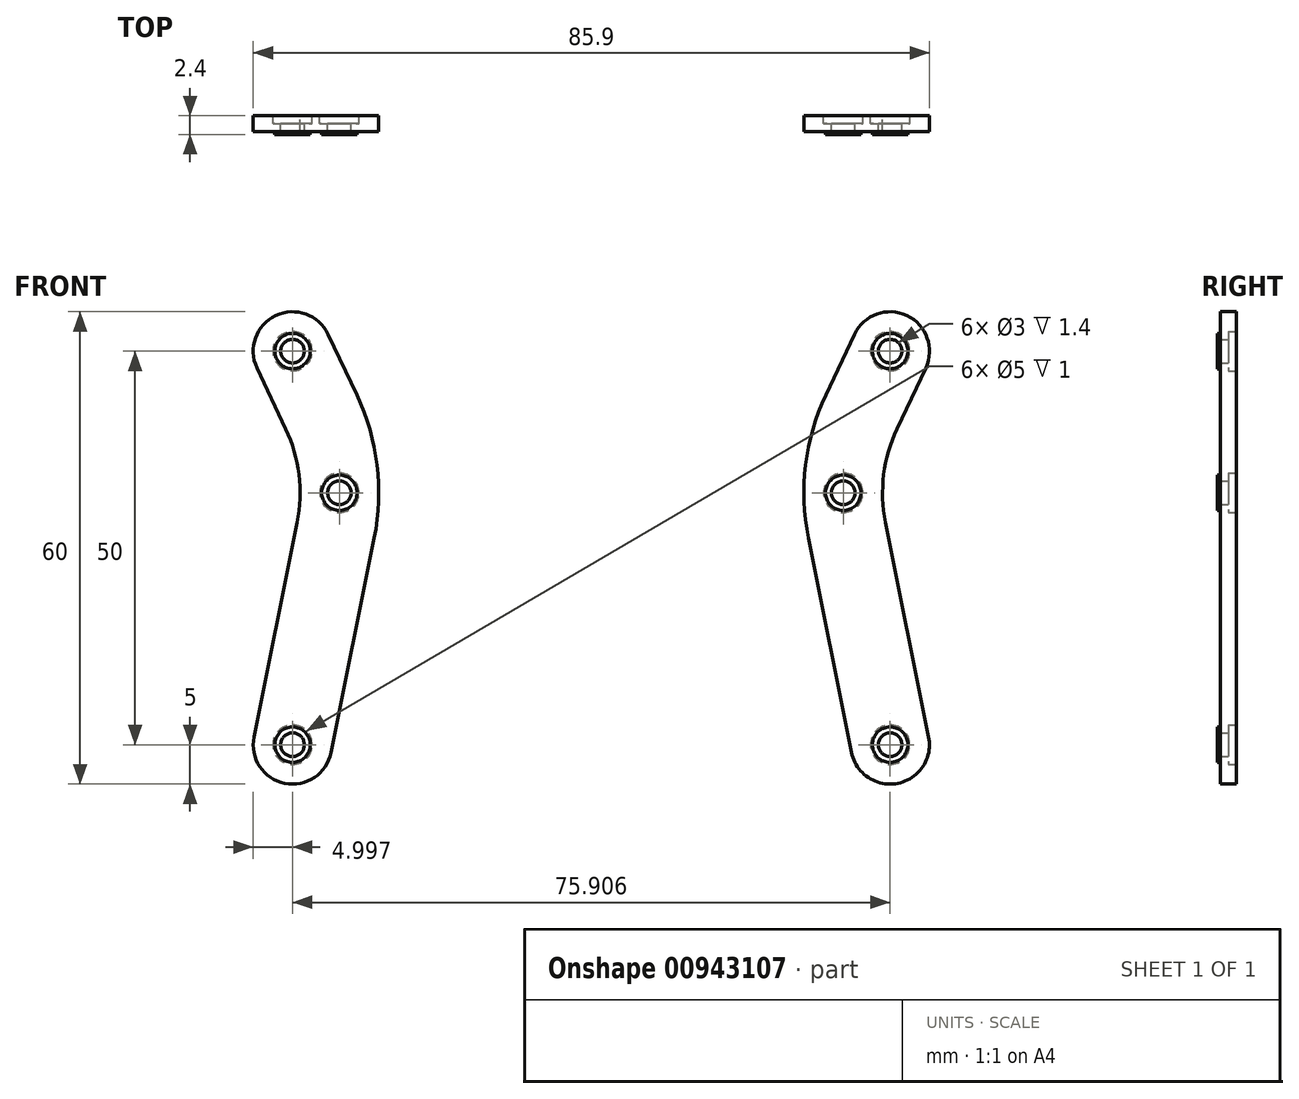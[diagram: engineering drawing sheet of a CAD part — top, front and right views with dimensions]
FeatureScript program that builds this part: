
annotation { "Feature Type Name" : "Feature", "Feature Type Description" : "" }
export const myFeature = defineFeature(function(context is Context, id is Id, definition is map)
    precondition{}
    {
        {
            var Q0;
            Q0=qCreatedBy(makeId("Front.planeOp"),FACE);
            var sketch = newSketch(context, id + "F0", { "sketchPlane" : qUnion([Q0])});
            skLineSegment(sketch, "E0", {"start": v(5.95, -32) * mm, "end": v(0.47, -4.74) * mm});
            skLineSegment(sketch, "E1", {"start": v(2.3, 10.26) * mm, "end": v(5.95, 18) * mm});
            skArc(sketch, "E2", {"start": v(2.3, 10.26) * mm, "mid": v(0.18, 2.9) * mm, "end": v(0.47, -4.74) * mm});
            skArc(sketch, "E3.0.left", {"start": v(6.82, 8.13) * mm, "mid": v(5.14, 2.3) * mm, "end": v(5.37, -3.75) * mm});
            skArc(sketch, "E3.0.right", {"start": v(-2.22, 12.4) * mm, "mid": v(-4.79, 3.51) * mm, "end": v(-4.43, -5.72) * mm});
            skArc(sketch, "E3.1.startCap", {"start": v(10.86, -31.01) * mm, "mid": v(6.94, -36.9) * mm, "end": v(1.05, -32.99) * mm});
            skLineSegment(sketch, "E3.1.left", {"start": v(1.05, -32.99) * mm, "end": v(-4.43, -5.72) * mm});
            skLineSegment(sketch, "E3.1.right", {"start": v(10.86, -31.01) * mm, "end": v(5.37, -3.75) * mm});
            skArc(sketch, "E3.2.endCap", {"start": v(1.43, 20.13) * mm, "mid": v(8.09, 22.52) * mm, "end": v(10.47, 15.87) * mm});
            skLineSegment(sketch, "E3.2.left", {"start": v(-2.22, 12.4) * mm, "end": v(1.43, 20.13) * mm});
            skLineSegment(sketch, "E3.2.right", {"start": v(6.82, 8.13) * mm, "end": v(10.47, 15.87) * mm});
            skPoint(sketch, "E4", {"position": v(0, 0) * mm});
            skSolve(sketch);
        }
        {
            var Q0;
            Q0=qSketchRegion(id+"F0",true);
            extrude(context, id + "F1", {"entities" : qUnion([Q0]), "depth" : 2 * mm, "offsetDistance" : 25 * mm});
        }
        {
            var Q0;
            Q0=sQuery(id+"F0.wireOp",VERTEX,"E1.end");
            var Q1;
            Q1=sQuery(id+"F0.wireOp",VERTEX,"E4");
            var Q2;
            Q2=sQuery(id+"F0.wireOp",VERTEX,"E0.start");
            var Q3;
            Q3=makeQuery(id+"F1.opExtrude","SWEPT_BODY",BODY,{"disambiguationData":[OSD([sQuery(id+"F0.wireOp",EDGE,"E3.0.left"),sQuery(id+"F0.wireOp",EDGE,"E3.0.right"),sQuery(id+"F0.wireOp",EDGE,"E3.1.startCap"),sQuery(id+"F0.wireOp",EDGE,"E3.1.left"),sQuery(id+"F0.wireOp",EDGE,"E3.1.right"),sQuery(id+"F0.wireOp",EDGE,"E3.2.endCap"),sQuery(id+"F0.wireOp",EDGE,"E3.2.left"),sQuery(id+"F0.wireOp",EDGE,"E3.2.right")])]});
            hole(context, id + "F2", {"style" : HoleStyle.C_BORE, "endStyle" : HoleEndStyle.THROUGH, "oppositeDirection" : true, "holeDiameter" : 3 * mm, "cBoreDiameter" : 5 * mm, "cBoreDepth" : 1 * mm, "majorDiameter" : 5 * mm, "isTappedThrough" : true, "tappedDepth" : 12 * mm, "tapClearance" : 3, "locations" : qUnion([Q0, Q1, Q2]), "scope" : qUnion([Q3])});
        }
        {
            var Q0;
            Q0=makeQuery(id+"F1.opExtrude","CAP_FACE",FACE,{"disambiguationData":[OSD([sQuery(id+"F0.wireOp",EDGE,"E3.0.left"),sQuery(id+"F0.wireOp",EDGE,"E3.0.right"),sQuery(id+"F0.wireOp",EDGE,"E3.1.startCap"),sQuery(id+"F0.wireOp",EDGE,"E3.1.left"),sQuery(id+"F0.wireOp",EDGE,"E3.1.right"),sQuery(id+"F0.wireOp",EDGE,"E3.2.endCap"),sQuery(id+"F0.wireOp",EDGE,"E3.2.left"),sQuery(id+"F0.wireOp",EDGE,"E3.2.right")])],"isStart":false});
            var sketch = newSketch(context, id + "F3", { "sketchPlane" : qUnion([Q0])});
            skCircle(sketch, "E5", {"center": v(5.95, 18) * mm, "radius": 2.25 * mm});
            skCircle(sketch, "E6", {"center": v(0, 0) * mm, "radius": 2.25 * mm});
            skCircle(sketch, "E7", {"center": v(5.95, -32) * mm, "radius": 2.25 * mm});
            skCircle(sketch, "E8", {"center": v(5.95, 18) * mm, "radius": 1.5 * mm});
            skCircle(sketch, "E9", {"center": v(0, 0) * mm, "radius": 1.5 * mm});
            skCircle(sketch, "E10", {"center": v(5.95, -32) * mm, "radius": 1.5 * mm});
            skSolve(sketch);
        }
        {
            var Q0;
            Q0=qSketchRegion(id+"F3",true);
            extrude(context, id + "F4", {"entities" : qUnion([Q0]), "operationType" : NewBodyOperationType.ADD, "depth" : 0.4 * mm, "offsetDistance" : 25 * mm});
        }
        {
            var Q0;
            Q0=makeQuery(id+"F1.opExtrude","CAP_FACE",FACE,{"disambiguationData":[OSD([sQuery(id+"F0.wireOp",EDGE,"E3.0.left"),sQuery(id+"F0.wireOp",EDGE,"E3.0.right"),sQuery(id+"F0.wireOp",EDGE,"E3.1.startCap"),sQuery(id+"F0.wireOp",EDGE,"E3.1.left"),sQuery(id+"F0.wireOp",EDGE,"E3.1.right"),sQuery(id+"F0.wireOp",EDGE,"E3.2.endCap"),sQuery(id+"F0.wireOp",EDGE,"E3.2.left"),sQuery(id+"F0.wireOp",EDGE,"E3.2.right")])],"isStart":false});
            var sketch = newSketch(context, id + "F5", { "sketchPlane" : qUnion([Q0])});
            skLineSegment(sketch, "E11", {"start": v(0.92, 7.33) * mm, "end": v(7.54, 21.35) * mm, "construction": true});
            skLineSegment(sketch, "E12", {"start": v(2.88, -16.7) * mm, "end": v(0.99, -7.31) * mm, "construction": true});
            skArc(sketch, "E13.0.startCap", {"start": v(3.18, 6.26) * mm, "mid": v(-0.15, 5.07) * mm, "end": v(-1.34, 8.4) * mm});
            skArc(sketch, "E13.0.endCap", {"start": v(5.27, 22.42) * mm, "mid": v(8.6, 23.61) * mm, "end": v(9.8, 20.28) * mm});
            skLineSegment(sketch, "E13.0.left", {"start": v(-1.34, 8.4) * mm, "end": v(5.27, 22.42) * mm});
            skLineSegment(sketch, "E13.0.right", {"start": v(3.18, 6.26) * mm, "end": v(9.8, 20.28) * mm});
            skArc(sketch, "E13.1.startCap", {"start": v(5.33, -16.2) * mm, "mid": v(3.37, -19.14) * mm, "end": v(0.42, -17.18) * mm});
            skArc(sketch, "E13.1.endCap", {"start": v(-1.46, -7.8) * mm, "mid": v(0.5, -4.86) * mm, "end": v(3.44, -6.82) * mm});
            skLineSegment(sketch, "E13.1.left", {"start": v(0.42, -17.18) * mm, "end": v(-1.46, -7.8) * mm});
            skLineSegment(sketch, "E13.1.right", {"start": v(5.33, -16.2) * mm, "end": v(3.44, -6.82) * mm});
            skSolve(sketch);
        }
        {
            var Q0;
            Q0=qCreatedBy(makeId("Right.planeOp"),FACE);
            cPlane(context, id + "F6", {"entities" : qUnion([Q0]), "cplaneType" : CPlaneType.OFFSET, "offset" : 32 * mm, "oppositeDirection" : true, "width" : 150 * mm, "height" : 150 * mm});
        }
        {
            var Q0;
            Q0=makeQuery(id+"F1.opExtrude","SWEPT_BODY",BODY,{"disambiguationData":[OSD([sQuery(id+"F0.wireOp",EDGE,"E3.0.left"),sQuery(id+"F0.wireOp",EDGE,"E3.0.right"),sQuery(id+"F0.wireOp",EDGE,"E3.1.startCap"),sQuery(id+"F0.wireOp",EDGE,"E3.1.left"),sQuery(id+"F0.wireOp",EDGE,"E3.1.right"),sQuery(id+"F0.wireOp",EDGE,"E3.2.endCap"),sQuery(id+"F0.wireOp",EDGE,"E3.2.left"),sQuery(id+"F0.wireOp",EDGE,"E3.2.right")])]});
            var Q1;
            Q1=qCreatedBy(id+"F6.planeOp",FACE);
            mirror(context, id + "F7", {"entities" : qUnion([Q0]), "mirrorPlane" : qUnion([Q1])});
        }
    });
